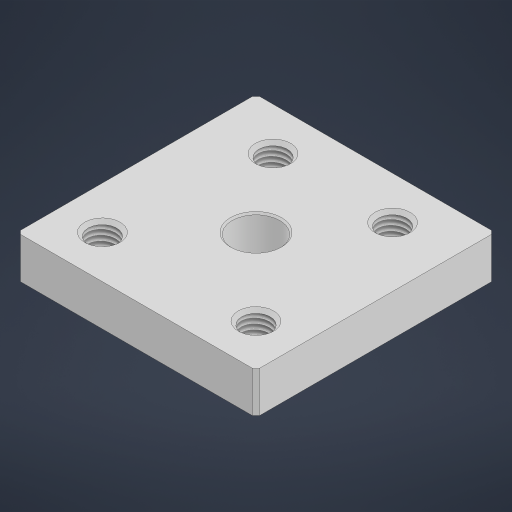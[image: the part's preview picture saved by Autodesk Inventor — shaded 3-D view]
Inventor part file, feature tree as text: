
AUTODESK INVENTOR PART (.ipt)
format: ipt  version: 2024.3 (Build 283343000, 343)  size: 213,504 bytes
history: native  units: mm
features: chamfer x3, sketch x1, extrude x1, hole x1
ambient origin geometry x8: Origin, YZ Plane, XZ Plane, XY Plane, X Axis, Y Axis, Z Axis, Center Point
bodies: Solid1 (feature_tree)
feature tree (6):
  sketch  "Sketch1"  dims[d0=70.0mm d1=45.0mm d2=14.0mm d3=12.0mm d4=0.0mm d5=8.376mm d6=20.0mm d7=4.0mm d8=2.0mm d9=90.0deg d10=7.0mm d11=0.0mm d13=1.0mm d14=2.0mm d15=45.0deg d16=0.5mm d17=2.0mm d18=45.0deg d19=70.0mm d20=35.0mm d21=45.0mm d22=1.0mm d23=2.0mm d24=45.0deg d25=12.5mm d26=17.5mm]
  extrude  "Extrusion1"  Depth=70.0mm
  hole  "Hole1"  [1 undecoded]
  chamfer  "Chamfer1"  Distance=12.0mm
  chamfer  "Chamfer2"  Distance=1.0mm Angle=45.0deg
  chamfer  "Chamfer3"  Distance=0.5mm Angle=45.0deg
note: 1 required parameter value undecoded (feature->parameter linkage not recoverable at this tier; creation-order binding heuristic only, values carry confidence <= 0.55)
